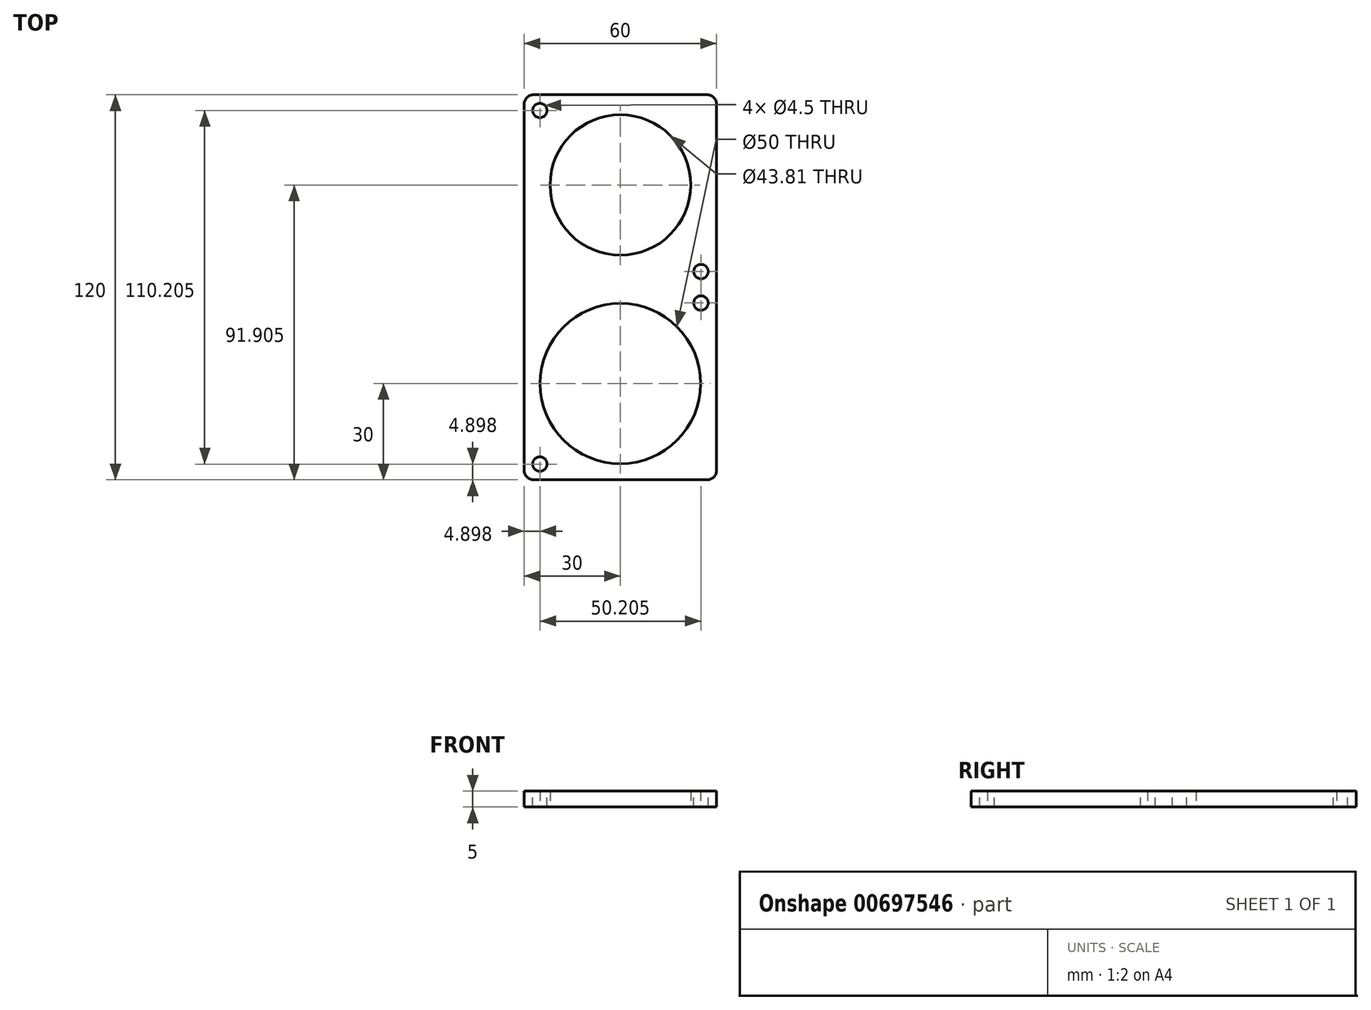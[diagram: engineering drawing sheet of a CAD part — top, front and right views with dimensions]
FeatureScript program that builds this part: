
annotation { "Feature Type Name" : "Feature", "Feature Type Description" : "" }
export const myFeature = defineFeature(function(context is Context, id is Id, definition is map)
    precondition{}
    {
        {
            var Q0;
            Q0=qCreatedBy(makeId("Top.planeOp"),FACE);
            var sketch = newSketch(context, id + "F0", { "sketchPlane" : qUnion([Q0])});
            skLineSegment(sketch, "E0.bottom", {"start": v(3, 0) * mm, "end": v(57, 0) * mm});
            skLineSegment(sketch, "E0.top", {"start": v(3, -120) * mm, "end": v(57, -120) * mm});
            skLineSegment(sketch, "E0.left", {"start": v(0, -3) * mm, "end": v(0, -117) * mm});
            skLineSegment(sketch, "E0.right", {"start": v(60, -3) * mm, "end": v(60, -117) * mm});
            skPoint(sketch, "E1.visualSharp", {"position": v(0, -120) * mm});
            skArc(sketch, "E1.filletArc", {"start": v(0, -117) * mm, "mid": v(0.88, -119.12) * mm, "end": v(3, -120) * mm});
            skPoint(sketch, "E2.visualSharp", {"position": v(60, -120) * mm});
            skArc(sketch, "E2.filletArc", {"start": v(57, -120) * mm, "mid": v(59.12, -119.12) * mm, "end": v(60, -117) * mm});
            skPoint(sketch, "E3.visualSharp", {"position": v(60, 0) * mm});
            skArc(sketch, "E3.filletArc", {"start": v(60, -3) * mm, "mid": v(59.12, -0.88) * mm, "end": v(57, 0) * mm});
            skPoint(sketch, "E4.visualSharp", {"position": v(0, 0) * mm});
            skArc(sketch, "E4.filletArc", {"start": v(3, 0) * mm, "mid": v(0.88, -0.88) * mm, "end": v(0, -3) * mm});
            skCircle(sketch, "E5", {"center": v(30, -90) * mm, "radius": 25 * mm});
            skCircle(sketch, "E6", {"center": v(30, -28.1) * mm, "radius": 21.9 * mm});
            skSolve(sketch);
        }
        {
            var Q0;
            Q0=makeQuery(id+"F0.imprint","IMPRINT",FACE,{"disambiguationData":[TD([[makeQuery(id+"F0.imprint","IMPRINT",EDGE,{"derivedFrom":sQuery(id+"F0.wireOp",EDGE,"E0.bottom")}),-1.0]])]});
            extrude(context, id + "F1", {"entities" : qUnion([Q0]), "depth" : 5 * mm, "offsetDistance" : 25 * mm});
        }
        {
            var Q0;
            Q0=makeQuery(id+"F1.opExtrude","CAP_FACE",FACE,{"disambiguationData":[OSD([sQuery(id+"F0.wireOp",EDGE,"E0.bottom"),sQuery(id+"F0.wireOp",EDGE,"E0.top"),sQuery(id+"F0.wireOp",EDGE,"E0.left"),sQuery(id+"F0.wireOp",EDGE,"E0.right"),sQuery(id+"F0.wireOp",EDGE,"E1.filletArc"),sQuery(id+"F0.wireOp",EDGE,"E2.filletArc"),sQuery(id+"F0.wireOp",EDGE,"E3.filletArc"),sQuery(id+"F0.wireOp",EDGE,"E4.filletArc"),sQuery(id+"F0.wireOp",EDGE,"E5"),sQuery(id+"F0.wireOp",EDGE,"E6")])],"isStart":false});
            var sketch = newSketch(context, id + "F2", { "sketchPlane" : qUnion([Q0])});
            skCircle(sketch, "E7", {"center": v(4.9, -115.1) * mm, "radius": 2.25 * mm});
            skCircle(sketch, "E8", {"center": v(55.1, -64.9) * mm, "radius": 2.25 * mm});
            skCircle(sketch, "E9", {"center": v(55.1, -55.1) * mm, "radius": 2.25 * mm});
            skCircle(sketch, "E10", {"center": v(4.9, -4.9) * mm, "radius": 2.25 * mm});
            skSolve(sketch);
        }
        {
            var Q0;
            Q0=makeQuery(id+"F2.imprint","IMPRINT",FACE,{"disambiguationData":[TD([[makeQuery(id+"F2.imprint","IMPRINT",EDGE,{"derivedFrom":sQuery(id+"F2.wireOp",EDGE,"E7")}),1.0]])]});
            var Q1;
            Q1=makeQuery(id+"F2.imprint","IMPRINT",FACE,{"disambiguationData":[TD([[makeQuery(id+"F2.imprint","IMPRINT",EDGE,{"derivedFrom":sQuery(id+"F2.wireOp",EDGE,"E8")}),1.0]])]});
            var Q2;
            Q2=makeQuery(id+"F2.imprint","IMPRINT",FACE,{"disambiguationData":[TD([[makeQuery(id+"F2.imprint","IMPRINT",EDGE,{"derivedFrom":sQuery(id+"F2.wireOp",EDGE,"E9")}),1.0]])]});
            var Q3;
            Q3=makeQuery(id+"F2.imprint","IMPRINT",FACE,{"disambiguationData":[TD([[makeQuery(id+"F2.imprint","IMPRINT",EDGE,{"derivedFrom":sQuery(id+"F2.wireOp",EDGE,"E10")}),1.0]])]});
            extrude(context, id + "F3", {"entities" : qUnion([Q0, Q1, Q2, Q3]), "operationType" : NewBodyOperationType.REMOVE, "oppositeDirection" : true, "depth" : 25 * mm, "offsetDistance" : 25 * mm});
        }
    });
